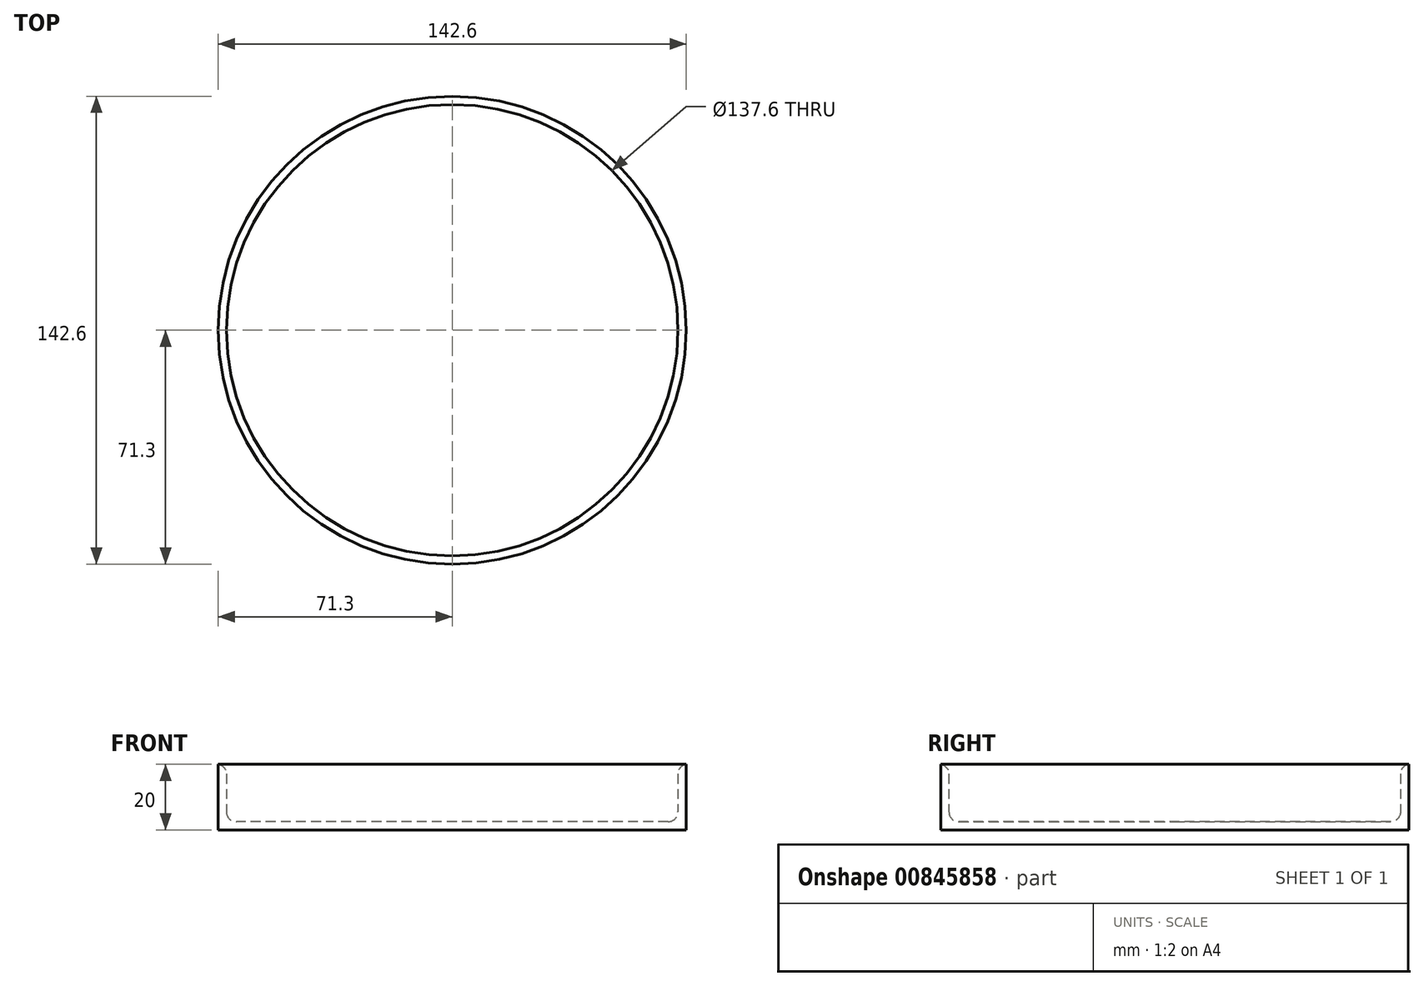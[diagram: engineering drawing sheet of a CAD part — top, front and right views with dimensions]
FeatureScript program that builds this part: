
annotation { "Feature Type Name" : "Feature", "Feature Type Description" : "" }
export const myFeature = defineFeature(function(context is Context, id is Id, definition is map)
    precondition{}
    {
        {
            var Q0;
            Q0=qCreatedBy(makeId("Top.planeOp"),FACE);
            var sketch = newSketch(context, id + "F0", { "sketchPlane" : qUnion([Q0])});
            skCircle(sketch, "E0", {"center": v(0, 0) * mm, "radius": 71.3 * mm});
            skSolve(sketch);
        }
        {
            var Q0;
            Q0=makeQuery(id+"F0.imprint","IMPRINT",FACE,{"disambiguationData":[TD([[makeQuery(id+"F0.imprint","IMPRINT",EDGE,{"derivedFrom":sQuery(id+"F0.wireOp",EDGE,"E0")}),1.0]])]});
            extrude(context, id + "F1", {"entities" : qUnion([Q0]), "depth" : 20 * mm, "offsetDistance" : 25 * mm});
        }
        {
            var Q0;
            Q0=makeQuery(id+"F1.opExtrude","CAP_FACE",FACE,{"disambiguationData":[OSD([sQuery(id+"F0.wireOp",EDGE,"E0")])],"isStart":false});
            shell(context, id + "F2", {"entities" : qUnion([Q0]), "thickness" : 2.5 * mm});
        }
        {
            var Q0;
            {var subQ0=sQuery(id+"F0.wireOp",EDGE,"E0");Q0=makeQuery(id+"F2.opShell","OFFSET_EDGE",EDGE,{"disambiguationData":[OSD([subQ0]),TDD([makeQuery(id+"F1.opExtrude","CAP_EDGE",EDGE,{"disambiguationData":[OSD([subQ0])],"isStart":true})])]});}
            fillet(context, id + "F3", {"entities" : qUnion([Q0]), "radius" : 3 * mm, "tangentPropagation" : true, "allowEdgeOverflow" : false});
        }
        {
            var Q0;
            {var subQ0=sQuery(id+"F0.wireOp",EDGE,"E0");Q0=makeQuery(id+"F2.opShell","OFFSET_EDGE",EDGE,{"disambiguationData":[OSD([subQ0]),TDD([makeQuery(id+"F1.opExtrude","CAP_EDGE",EDGE,{"disambiguationData":[OSD([subQ0])],"isStart":false})])]});}
            fillet(context, id + "F4", {"entities" : qUnion([Q0]), "radius" : 3 * mm, "tangentPropagation" : true, "allowEdgeOverflow" : false});
        }
    });
